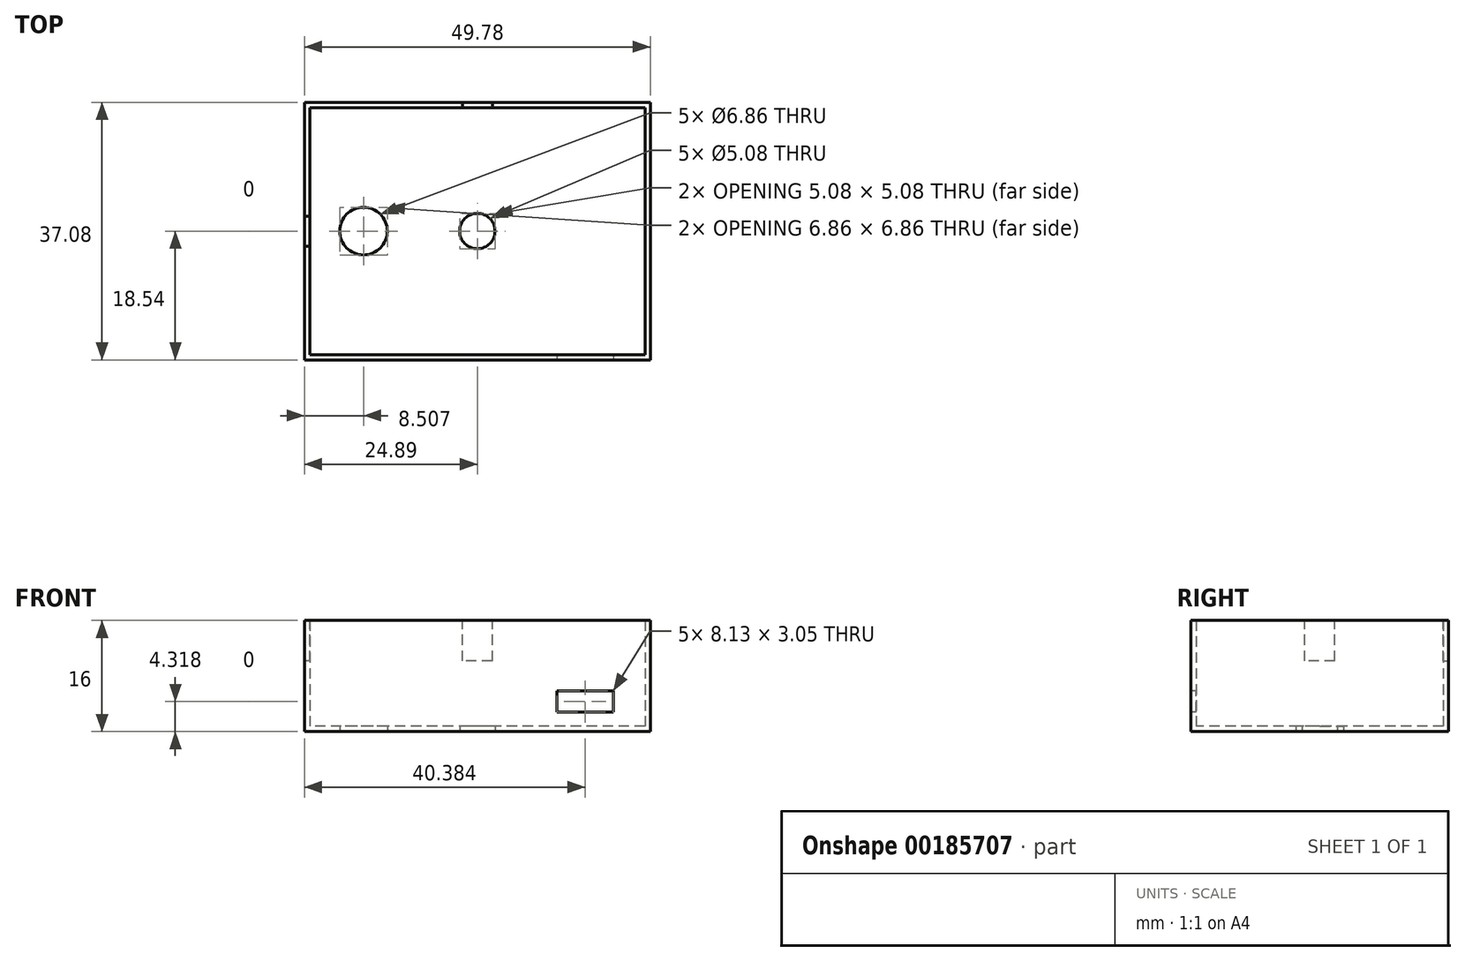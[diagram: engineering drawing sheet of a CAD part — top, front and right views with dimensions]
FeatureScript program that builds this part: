
annotation { "Feature Type Name" : "Feature", "Feature Type Description" : "" }
export const myFeature = defineFeature(function(context is Context, id is Id, definition is map)
    precondition{}
    {
        {
            var Q0;
            Q0=qCreatedBy(makeId("Top.planeOp"),FACE);
            var sketch = newSketch(context, id + "F0", { "sketchPlane" : qUnion([Q0])});
            skLineSegment(sketch, "E0.bottom", {"start": v(24.9, 18.54) * mm, "end": v(-24.9, 18.54) * mm});
            skLineSegment(sketch, "E0.top", {"start": v(24.9, -18.54) * mm, "end": v(-24.9, -18.54) * mm});
            skLineSegment(sketch, "E0.left", {"start": v(24.9, 18.54) * mm, "end": v(24.9, -18.54) * mm});
            skLineSegment(sketch, "E0.right", {"start": v(-24.9, 18.54) * mm, "end": v(-24.9, -18.54) * mm});
            skPoint(sketch, "E0.middle", {"position": v(0, 0) * mm});
            skCircle(sketch, "E1", {"center": v(0, 0) * mm, "radius": 2.92 * mm});
            skLineSegment(sketch, "E2", {"start": v(-24.9, 0) * mm, "end": v(-16.38, 0) * mm});
            skPoint(sketch, "E2.endSnap0", {"position": v(-24.9, 0) * mm});
            skCircle(sketch, "E3", {"center": v(-16.38, 0) * mm, "radius": 3.81 * mm});
            skSolve(sketch);
        }
        {
            var Q0;
            Q0=makeQuery(id+"F0.imprint","IMPRINT",FACE,{"disambiguationData":[TD([[makeQuery(id+"F0.imprint","IMPRINT",EDGE,{"derivedFrom":sQuery(id+"F0.wireOp",EDGE,"E3")}),1.0]])]});
            var Q1;
            {var subQ1=sQuery(id+"F0.wireOp",EDGE,"E0.bottom");Q1=makeQuery(id+"F0.imprint","IMPRINT",FACE,{"disambiguationData":[TD([[makeQuery(id+"F0.imprint","IMPRINT",EDGE,{"derivedFrom":subQ1}),1.0]])]});}
            var Q2;
            Q2=makeQuery(id+"F0.imprint","IMPRINT",FACE,{"disambiguationData":[TD([[makeQuery(id+"F0.imprint","IMPRINT",EDGE,{"derivedFrom":sQuery(id+"F0.wireOp",EDGE,"E1")}),1.0]])]});
            extrude(context, id + "F1", {"entities" : qUnion([Q0, Q1, Q2]), "depth" : 16 * mm});
        }
        {
            var Q0;
            Q0=makeQuery(id+"F1.opExtrude","CAP_FACE",FACE,{"disambiguationData":[OSD([sQuery(id+"F0.wireOp",EDGE,"E0.bottom"),sQuery(id+"F0.wireOp",EDGE,"E0.top"),sQuery(id+"F0.wireOp",EDGE,"E0.left"),sQuery(id+"F0.wireOp",EDGE,"E0.right")])],"isStart":false});
            shell(context, id + "F2", {"entities" : qUnion([Q0]), "thickness" : 0.76 * mm});
        }
        {
            var Q0;
            Q0=sQuery(id+"F0.wireOp",VERTEX,"E2.end");
            var Q1;
            Q1=makeQuery(id+"F1.opExtrude","SWEPT_BODY",BODY,{"disambiguationData":[OSD([sQuery(id+"F0.wireOp",EDGE,"E0.bottom"),sQuery(id+"F0.wireOp",EDGE,"E0.top"),sQuery(id+"F0.wireOp",EDGE,"E0.left"),sQuery(id+"F0.wireOp",EDGE,"E0.right")])]});
            hole(context, id + "F3", {"style" : HoleStyle.SIMPLE, "endStyle" : HoleEndStyle.THROUGH, "oppositeDirection" : true, "holeDiameter" : 6.86 * mm, "locations" : qUnion([Q0]), "scope" : qUnion([Q1]), "isTappedThrough" : true});
        }
        {
            var Q0;
            Q0=sQuery(id+"F0.wireOp",VERTEX,"E0.middle");
            var Q1;
            Q1=makeQuery(id+"F1.opExtrude","SWEPT_BODY",BODY,{"disambiguationData":[OSD([sQuery(id+"F0.wireOp",EDGE,"E0.bottom"),sQuery(id+"F0.wireOp",EDGE,"E0.top"),sQuery(id+"F0.wireOp",EDGE,"E0.left"),sQuery(id+"F0.wireOp",EDGE,"E0.right")])]});
            hole(context, id + "F4", {"style" : HoleStyle.SIMPLE, "endStyle" : HoleEndStyle.THROUGH, "oppositeDirection" : true, "holeDiameter" : 5.08 * mm, "locations" : qUnion([Q0]), "scope" : qUnion([Q1]), "isTappedThrough" : true});
        }
        {
            var Q0;
            Q0=makeQuery(id+"F1.opExtrude","SWEPT_FACE",FACE,{"disambiguationData":[OSD([sQuery(id+"F0.wireOp",EDGE,"E0.top")])]});
            var sketch = newSketch(context, id + "F5", { "sketchPlane" : qUnion([Q0])});
            skLineSegment(sketch, "E4.bottom", {"start": v(24.9, 0) * mm, "end": v(19.56, 0) * mm});
            skLineSegment(sketch, "E4.top", {"start": v(24.9, 2.8) * mm, "end": v(19.56, 2.8) * mm});
            skLineSegment(sketch, "E4.left", {"start": v(24.9, 0) * mm, "end": v(24.9, 2.8) * mm});
            skLineSegment(sketch, "E4.right", {"start": v(19.56, 0) * mm, "end": v(19.56, 2.8) * mm});
            skLineSegment(sketch, "E5.bottom", {"start": v(19.56, 2.8) * mm, "end": v(11.43, 2.8) * mm});
            skLineSegment(sketch, "E5.top", {"start": v(19.56, 5.84) * mm, "end": v(11.43, 5.84) * mm});
            skLineSegment(sketch, "E5.left", {"start": v(19.56, 2.8) * mm, "end": v(19.56, 5.84) * mm});
            skLineSegment(sketch, "E5.right", {"start": v(11.43, 2.8) * mm, "end": v(11.43, 5.84) * mm});
            skSolve(sketch);
        }
        {
            var Q0;
            Q0=makeQuery(id+"F5.imprint","IMPRINT",FACE,{"disambiguationData":[TD([[makeQuery(id+"F5.imprint","IMPRINT",EDGE,{"derivedFrom":sQuery(id+"F5.wireOp",EDGE,"E5.bottom")}),-1.0]])]});
            extrude(context, id + "F6", {"entities" : qUnion([Q0]), "operationType" : NewBodyOperationType.REMOVE, "oppositeDirection" : true, "depth" : 25.4 * mm});
        }
        {
            var Q0;
            Q0=makeQuery(id+"F1.opExtrude","SWEPT_FACE",FACE,{"disambiguationData":[OSD([sQuery(id+"F0.wireOp",EDGE,"E0.bottom")])]});
            var sketch = newSketch(context, id + "F7", { "sketchPlane" : qUnion([Q0])});
            skLineSegment(sketch, "E6", {"start": v(0, 16) * mm, "end": v(0, 13.08) * mm});
            skPoint(sketch, "E6.endSnap0", {"position": v(0, 16) * mm});
            skLineSegment(sketch, "E7.bottom", {"start": v(2.16, 16) * mm, "end": v(-2.16, 16) * mm});
            skLineSegment(sketch, "E7.top", {"start": v(2.16, 10.16) * mm, "end": v(-2.16, 10.16) * mm});
            skLineSegment(sketch, "E7.left", {"start": v(2.16, 16) * mm, "end": v(2.16, 10.16) * mm});
            skLineSegment(sketch, "E7.right", {"start": v(-2.16, 16) * mm, "end": v(-2.16, 10.16) * mm});
            skPoint(sketch, "E7.middle", {"position": v(0, 13.08) * mm});
            skSolve(sketch);
        }
        {
            var Q0;
            Q0=qSketchRegion(id+"F7",true);
            extrude(context, id + "F8", {"entities" : qUnion([Q0]), "operationType" : NewBodyOperationType.REMOVE, "oppositeDirection" : true, "depth" : 25.4 * mm});
        }
        {
            var Q0;
            Q0=makeQuery(id+"F1.opExtrude","SWEPT_FACE",FACE,{"disambiguationData":[OSD([sQuery(id+"F0.wireOp",EDGE,"E0.right")])]});
            var sketch = newSketch(context, id + "F9", { "sketchPlane" : qUnion([Q0])});
            skLineSegment(sketch, "E8", {"start": v(0, 16) * mm, "end": v(0, 13.08) * mm});
            skPoint(sketch, "E8.endSnap0", {"position": v(0, 16) * mm});
            skLineSegment(sketch, "E9.bottom", {"start": v(2.16, 16) * mm, "end": v(-2.16, 16) * mm});
            skLineSegment(sketch, "E9.top", {"start": v(2.16, 10.16) * mm, "end": v(-2.16, 10.16) * mm});
            skLineSegment(sketch, "E9.left", {"start": v(2.16, 16) * mm, "end": v(2.16, 10.16) * mm});
            skLineSegment(sketch, "E9.right", {"start": v(-2.16, 16) * mm, "end": v(-2.16, 10.16) * mm});
            skPoint(sketch, "E9.middle", {"position": v(0, 13.08) * mm});
            skSolve(sketch);
        }
        {
            var Q0;
            Q0=makeQuery(id+"F9.imprint","IMPRINT",FACE,{"disambiguationData":[TD([[makeQuery(id+"F9.imprint","IMPRINT",EDGE,{"derivedFrom":sQuery(id+"F9.wireOp",EDGE,"E9.top")}),-1.0]])]});
            extrude(context, id + "F10", {"entities" : qUnion([Q0]), "operationType" : NewBodyOperationType.REMOVE, "oppositeDirection" : true, "depth" : 25.4 * mm});
        }
    });
